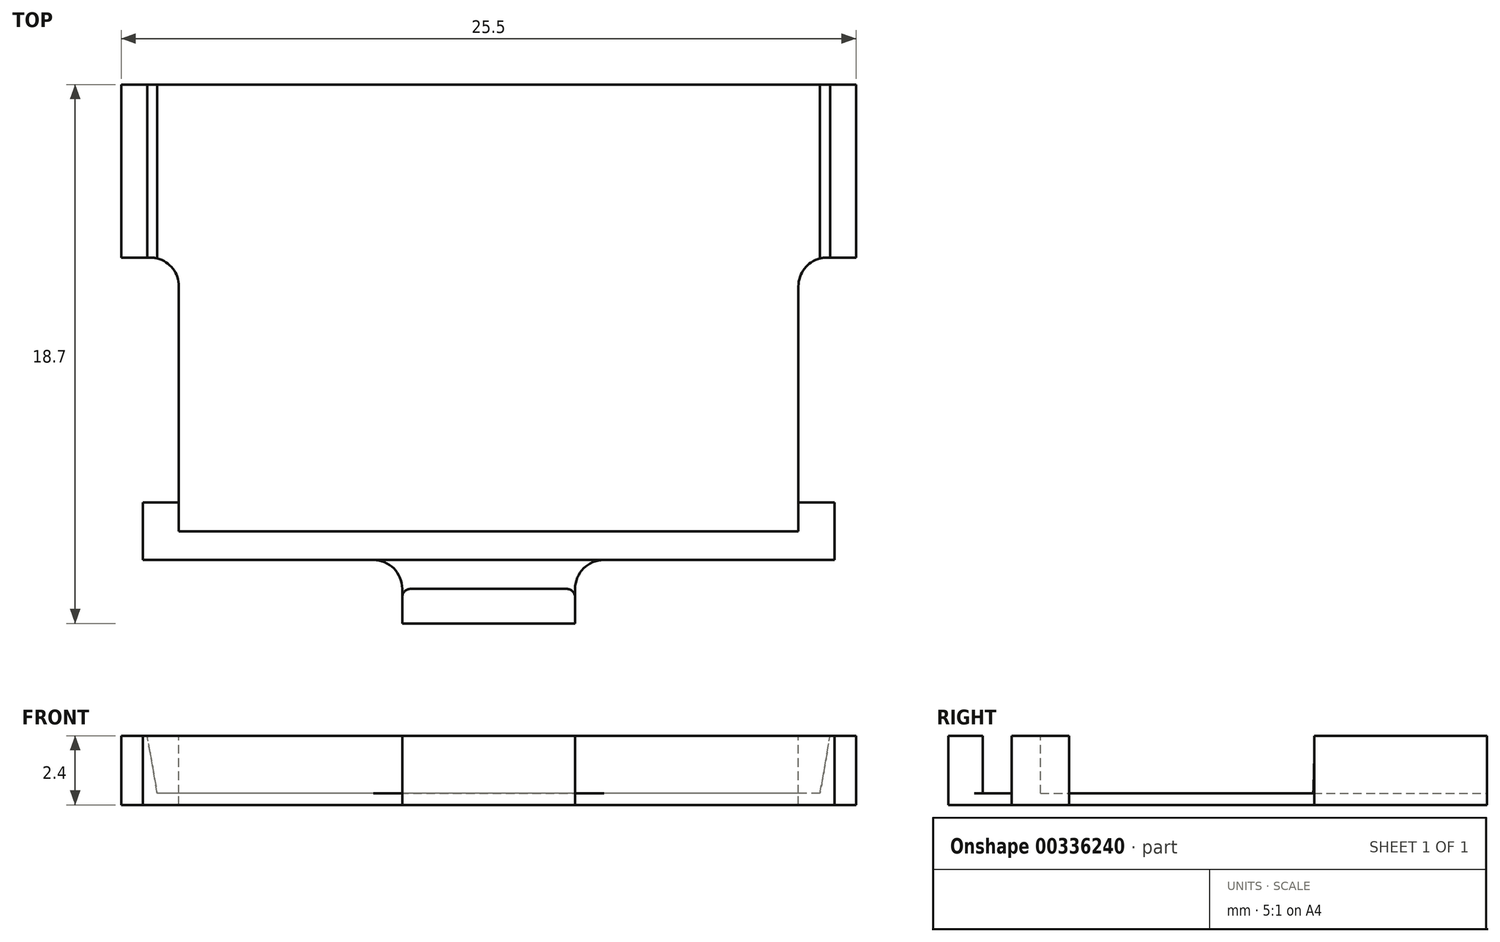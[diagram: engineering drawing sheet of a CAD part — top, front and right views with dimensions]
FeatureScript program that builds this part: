
annotation { "Feature Type Name" : "Feature", "Feature Type Description" : "" }
export const myFeature = defineFeature(function(context is Context, id is Id, definition is map)
    precondition{}
    {
        {
            var Q0;
            Q0=qCreatedBy(makeId("Top.planeOp"),FACE);
            var sketch = newSketch(context, id + "F0", { "sketchPlane" : qUnion([Q0])});
            skLineSegment(sketch, "E0.bottom", {"start": v(-10.75, 0) * mm, "end": v(10.75, 0) * mm});
            skLineSegment(sketch, "E0.top", {"start": v(-10.75, 16.5) * mm, "end": v(10.75, 16.5) * mm});
            skLineSegment(sketch, "E0.left", {"start": v(-10.75, 0) * mm, "end": v(-10.75, 16.5) * mm});
            skLineSegment(sketch, "E0.right", {"start": v(10.75, 0) * mm, "end": v(10.75, 16.5) * mm});
            skLineSegment(sketch, "E1", {"start": v(-10.75, 0) * mm, "end": v(-12, 0) * mm});
            skLineSegment(sketch, "E2", {"start": v(-12, 0) * mm, "end": v(-12, 2) * mm});
            skLineSegment(sketch, "E3", {"start": v(-12, 2) * mm, "end": v(-10.75, 2) * mm});
            skLineSegment(sketch, "E4.MirrorCS", {"start": v(12, 2) * mm, "end": v(10.75, 2) * mm});
            skLineSegment(sketch, "E5.MirrorCS", {"start": v(12, 0) * mm, "end": v(12, 2) * mm});
            skLineSegment(sketch, "E6.MirrorCS", {"start": v(10.75, 0) * mm, "end": v(12, 0) * mm});
            skLineSegment(sketch, "E7", {"start": v(-10.75, 2) * mm, "end": v(10.75, 2) * mm, "construction": true});
            skLineSegment(sketch, "E8", {"start": v(-10.75, 16.5) * mm, "end": v(-11.85, 16.5) * mm});
            skLineSegment(sketch, "E9", {"start": v(-11.85, 16.5) * mm, "end": v(-11.85, 10.5) * mm});
            skLineSegment(sketch, "E10", {"start": v(-11.85, 10.5) * mm, "end": v(-10.75, 10.5) * mm});
            skLineSegment(sketch, "E11", {"start": v(-11.85, 16.5) * mm, "end": v(-12.75, 16.5) * mm});
            skLineSegment(sketch, "E12", {"start": v(-12.75, 16.5) * mm, "end": v(-12.75, 10.5) * mm});
            skLineSegment(sketch, "E13", {"start": v(-12.75, 10.5) * mm, "end": v(-11.85, 10.5) * mm});
            skLineSegment(sketch, "E14.MirrorCS", {"start": v(10.75, 16.5) * mm, "end": v(11.85, 16.5) * mm});
            skLineSegment(sketch, "E15.MirrorCS", {"start": v(11.85, 10.5) * mm, "end": v(10.75, 10.5) * mm});
            skLineSegment(sketch, "E16.MirrorCS", {"start": v(11.85, 16.5) * mm, "end": v(11.85, 10.5) * mm});
            skLineSegment(sketch, "E17.MirrorCS", {"start": v(11.85, 16.5) * mm, "end": v(12.75, 16.5) * mm});
            skLineSegment(sketch, "E18.MirrorCS", {"start": v(12.75, 10.5) * mm, "end": v(11.85, 10.5) * mm});
            skLineSegment(sketch, "E19.MirrorCS", {"start": v(12.75, 16.5) * mm, "end": v(12.75, 10.5) * mm});
            skLineSegment(sketch, "E20", {"start": v(-10.75, 1) * mm, "end": v(10.75, 1) * mm});
            skPoint(sketch, "E20.startSnap0", {"position": v(-12, 1) * mm});
            skLineSegment(sketch, "E21", {"start": v(-3, 0) * mm, "end": v(-3, -1) * mm});
            skLineSegment(sketch, "E22", {"start": v(-3, -1) * mm, "end": v(3, -1) * mm});
            skLineSegment(sketch, "E23", {"start": v(3, -1) * mm, "end": v(3, 0) * mm});
            skLineSegment(sketch, "E24", {"start": v(-3, -1) * mm, "end": v(-3, -2.2) * mm});
            skLineSegment(sketch, "E25", {"start": v(-3, -2.2) * mm, "end": v(3, -2.2) * mm});
            skLineSegment(sketch, "E26", {"start": v(3, -2.2) * mm, "end": v(3, -1) * mm});
            skSolve(sketch);
        }
        {
            var Q0;
            Q0=qCreatedBy(makeId("Front.planeOp"),FACE);
            var sketch = newSketch(context, id + "F1", { "sketchPlane" : qUnion([Q0])});
            skLineSegment(sketch, "E27", {"start": v(0, 0) * mm, "end": v(0, 0.4) * mm});
            skLineSegment(sketch, "E28", {"start": v(0, 0.4) * mm, "end": v(0, 2.4) * mm});
            skSolve(sketch);
        }
        {
            var Q0;
            Q0 = qSketchRegion(id + "F0", true);
            var Q1;
            Q1=sQuery(id+"F1.wireOp",EDGE,"E27");
            sweep(context, id + "F2", {"profiles" : qUnion([Q0]), "path" : qUnion([Q1])});
        }
        {
            var Q0;
            {var subQ0=sQuery(id+"F0.wireOp",EDGE,"E0.bottom");Q0=makeQuery(id+"F0.imprint","IMPRINT",FACE,{"disambiguationData":[TD([[makeQuery(id+"F0.imprint","IMPRINT",EDGE,{"derivedFrom":subQ0}),1.0]])]});}
            var Q1;
            {var subQ0=sQuery(id+"F0.wireOp",EDGE,"E1");Q1=makeQuery(id+"F0.imprint","IMPRINT",FACE,{"disambiguationData":[TD([[makeQuery(id+"F0.imprint","IMPRINT",EDGE,{"derivedFrom":subQ0}),-1.0]])]});}
            var Q2;
            {var subQ2=sQuery(id+"F0.wireOp",EDGE,"E4.MirrorCS");Q2=makeQuery(id+"F0.imprint","IMPRINT",FACE,{"disambiguationData":[TD([[makeQuery(id+"F0.imprint","IMPRINT",EDGE,{"derivedFrom":subQ2}),1.0]])]});}
            var Q3;
            Q3=makeQuery(id+"F0.imprint","IMPRINT",FACE,{"disambiguationData":[TD([[makeQuery(id+"F0.imprint","IMPRINT",EDGE,{"derivedFrom":sQuery(id+"F0.wireOp",EDGE,"E16.MirrorCS")}),1.0]])]});
            var Q4;
            Q4=makeQuery(id+"F0.imprint","IMPRINT",FACE,{"disambiguationData":[TD([[makeQuery(id+"F0.imprint","IMPRINT",EDGE,{"derivedFrom":sQuery(id+"F0.wireOp",EDGE,"E9")}),-1.0]])]});
            var Q5;
            Q5=makeQuery(id+"F0.imprint","IMPRINT",FACE,{"disambiguationData":[TD([[makeQuery(id+"F0.imprint","IMPRINT",EDGE,{"derivedFrom":sQuery(id+"F0.wireOp",EDGE,"E22")}),-1.0]])]});
            var Q6;
            Q6=sQuery(id+"F1.wireOp",EDGE,"E27");
            var Q7;
            Q7=sQuery(id+"F1.wireOp",EDGE,"E28");
            sweep(context, id + "F3", {"operationType" : NewBodyOperationType.ADD, "profiles" : qUnion([Q0, Q1, Q2, Q3, Q4, Q5]), "path" : qUnion([Q6, Q7])});
        }
        {
            var Q0;
            {var subQ0=sQuery(id+"F1.wireOp",EDGE,"E27");var subQ1=sQuery(id+"F0.wireOp",EDGE,"E17.MirrorCS");var subQ2=sQuery(id+"F0.wireOp",EDGE,"E11");Q0=makeQuery(id+"F3.boolean.opBoolean","MERGE",FACE,{"derivedFrom":[makeQuery(id+"F2.opSweep","SWEPT_FACE",FACE,{"disambiguationData":[OSD([sQuery(id+"F0.wireOp",EDGE,"E0.top"),sQuery(id+"F0.wireOp",EDGE,"E8"),subQ2,sQuery(id+"F0.wireOp",EDGE,"E14.MirrorCS"),subQ1,subQ0])]}),makeQuery(id+"F3.opSweep","SWEPT_FACE",FACE,{"disambiguationData":[OSD([subQ2,subQ0])]}),makeQuery(id+"F3.opSweep","SWEPT_FACE",FACE,{"disambiguationData":[OSD([subQ1,subQ0])]})]});}
            var sketch = newSketch(context, id + "F4", { "sketchPlane" : qUnion([Q0])});
            skLineSegment(sketch, "E29", {"start": v(-11.5, 0.4) * mm, "end": v(11.5, 0.4) * mm, "construction": true});
            skLineSegment(sketch, "E30", {"start": v(-11.85, 2.4) * mm, "end": v(-11.85, 0.4) * mm});
            skLineSegment(sketch, "E31", {"start": v(-11.85, 0.4) * mm, "end": v(-11.5, 0.4) * mm});
            skLineSegment(sketch, "E32", {"start": v(-11.5, 0.4) * mm, "end": v(-11.85, 2.4) * mm});
            skLineSegment(sketch, "E33.MirrorCS", {"start": v(11.5, 0.4) * mm, "end": v(11.85, 2.4) * mm});
            skLineSegment(sketch, "E34.MirrorCS", {"start": v(11.85, 0.4) * mm, "end": v(11.5, 0.4) * mm});
            skLineSegment(sketch, "E35.MirrorCS", {"start": v(11.85, 2.4) * mm, "end": v(11.85, 0.4) * mm});
            skSolve(sketch);
        }
        {
            var Q0;
            Q0 = qSketchRegion(id + "F4", true);
            var Q1;
            {var subQ0=sQuery(id+"F1.wireOp",EDGE,"E27");var subQ1=sQuery(id+"F0.wireOp",EDGE,"E18.MirrorCS");Q1=makeQuery(id+"F3.boolean.opBoolean","MERGE",FACE,{"derivedFrom":[makeQuery(id+"F2.opSweep","SWEPT_FACE",FACE,{"disambiguationData":[OSD([sQuery(id+"F0.wireOp",EDGE,"E15.MirrorCS"),subQ1,subQ0])]}),makeQuery(id+"F3.opSweep","SWEPT_FACE",FACE,{"disambiguationData":[OSD([subQ1,subQ0])]})]});}
            extrude(context, id + "F5", {"entities" : qUnion([Q0]), "operationType" : NewBodyOperationType.ADD, "endBound" : BoundingType.UP_TO_SURFACE, "oppositeDirection" : true, "depth" : 25 * mm, "endBoundEntityFace" : qUnion([Q1]), "offsetDistance" : 25 * mm});
        }
        {
            var Q0;
            Q0=makeQuery(id+"F2.opSweep","SWEPT_EDGE",EDGE,{"disambiguationData":[OSD([sQuery(id+"F0.wireOp",EDGE,"E0.bottom"),sQuery(id+"F0.wireOp",EDGE,"E23"),sQuery(id+"F1.wireOp",EDGE,"E27")])]});
            var Q1;
            Q1=makeQuery(id+"F2.opSweep","SWEPT_EDGE",EDGE,{"disambiguationData":[OSD([sQuery(id+"F0.wireOp",EDGE,"E0.bottom"),sQuery(id+"F0.wireOp",EDGE,"E21"),sQuery(id+"F1.wireOp",EDGE,"E27")])]});
            var Q2;
            Q2=makeQuery(id+"F2.opSweep","SWEPT_EDGE",EDGE,{"disambiguationData":[OSD([sQuery(id+"F0.wireOp",EDGE,"E0.right"),sQuery(id+"F0.wireOp",EDGE,"E15.MirrorCS"),sQuery(id+"F1.wireOp",EDGE,"E27")])]});
            var Q3;
            Q3=makeQuery(id+"F2.opSweep","SWEPT_EDGE",EDGE,{"disambiguationData":[OSD([sQuery(id+"F0.wireOp",EDGE,"E0.left"),sQuery(id+"F0.wireOp",EDGE,"E10"),sQuery(id+"F1.wireOp",EDGE,"E27")])]});
            fillet(context, id + "F6", {"entities" : qUnion([Q0, Q1, Q2, Q3]), "radius" : 1 * mm, "allowEdgeOverflow" : false});
        }
        {
            var Q0;
            Q0=makeQuery(id+"F3.opSweep","SWEPT_EDGE",EDGE,{"disambiguationData":[OSD([sQuery(id+"F0.wireOp",EDGE,"E21"),sQuery(id+"F0.wireOp",EDGE,"E22"),sQuery(id+"F0.wireOp",EDGE,"E24"),sQuery(id+"F1.wireOp",EDGE,"E27")])]});
            var Q1;
            Q1=makeQuery(id+"F3.opSweep","SWEPT_EDGE",EDGE,{"disambiguationData":[OSD([sQuery(id+"F0.wireOp",EDGE,"E22"),sQuery(id+"F0.wireOp",EDGE,"E23"),sQuery(id+"F0.wireOp",EDGE,"E26"),sQuery(id+"F1.wireOp",EDGE,"E27")])]});
            fillet(context, id + "F7", {"entities" : qUnion([Q0, Q1]), "radius" : 0.3 * mm, "allowEdgeOverflow" : false});
        }
    });
